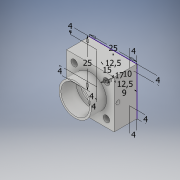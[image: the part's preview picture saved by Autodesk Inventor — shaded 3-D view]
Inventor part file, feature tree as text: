
AUTODESK INVENTOR PART (.ipt)
format: ipt  version: 2019 (Build 230136000, 136)  size: 195,072 bytes
history: native  units: mm
features: extrude x3, sketch x2, hole x2
ambient origin geometry x8: Origin, YZ Plane, XZ Plane, XY Plane, X Axis, Y Axis, Z Axis, Center Point
bodies: Volumenkörper3 (feature_tree), Volumenkörper4 (feature_tree)
feature tree (7):
  sketch  "Skizze1"  dims[d0=25.0mm d1=25.0mm]
  sketch  "Skizze2"  dims[d2=4.0mm d3=4.0mm d4=4.0mm d5=4.0mm d6=10.0mm d7=15.0mm d8=17.0mm d11=9.0mm d12=20.0mm d13=0.0mm d14=12.0mm d15=0.0mm d16=6.4mm d17=0.0mm d18=12.5mm d19=12.5mm d21=4.0mm d29=3.4mm d30=8.0mm d31=6.5mm d32=3.4mm d33=90.0deg d34=8.0mm d35=20.594885mm d38=4.0mm d39=4.0mm d40=2.057mm d41=6.0mm d42=8.0mm d43=4.5mm d44=90.0deg d45=8.0mm d46=20.594885mm d47=10.0mm d48=4.0mm d22=1.0mm d23=1.0mm d24=1.0mm d25=0.15mm d26=0.25mm d27=0.375mm d28=14.3117mm]
  extrude  "Extrusion2"  Depth=25.0mm
  extrude  "Extrusion3"  Depth=10.0mm
  extrude  "Extrusion4"  Depth=10.0mm
  hole  "Bohrung2"  [1 undecoded]
  hole  "Bohrung3"  [1 undecoded]
note: 2 required parameter values undecoded (feature->parameter linkage not recoverable at this tier; creation-order binding heuristic only, values carry confidence <= 0.55)
